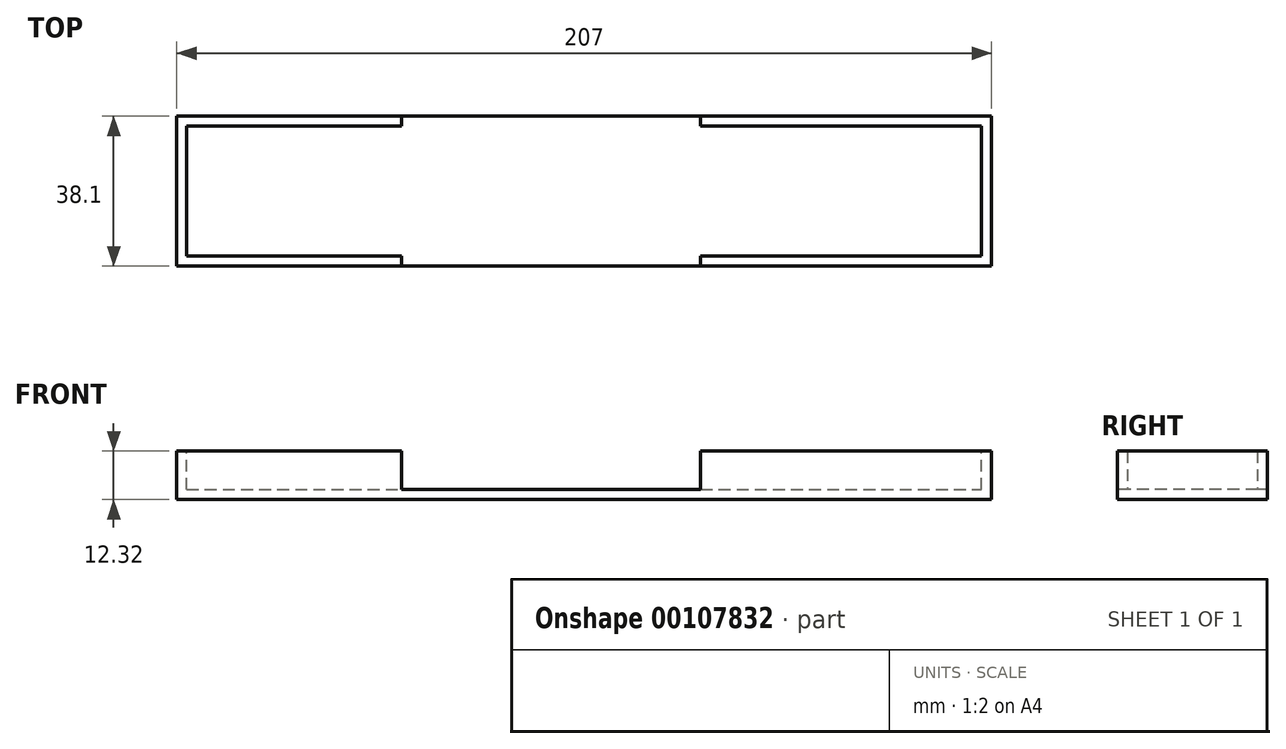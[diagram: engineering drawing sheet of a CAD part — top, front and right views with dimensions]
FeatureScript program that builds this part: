
annotation { "Feature Type Name" : "Feature", "Feature Type Description" : "" }
export const myFeature = defineFeature(function(context is Context, id is Id, definition is map)
    precondition{}
    {
        {
            var Q0;
            Q0=qCreatedBy(makeId("Front.planeOp"),FACE);
            var sketch = newSketch(context, id + "F0", { "sketchPlane" : qUnion([Q0])});
            skLineSegment(sketch, "E0.bottom", {"start": v(103.5, -6.16) * mm, "end": v(-103.5, -6.16) * mm});
            skLineSegment(sketch, "E0.left", {"start": v(103.5, -6.16) * mm, "end": v(103.5, 6.16) * mm});
            skLineSegment(sketch, "E0.right", {"start": v(-103.5, -6.16) * mm, "end": v(-103.5, 6.16) * mm});
            skPoint(sketch, "E0.middle", {"position": v(0, 0) * mm});
            skLineSegment(sketch, "E1", {"start": v(-103.5, 6.16) * mm, "end": v(-46.35, 6.16) * mm});
            skLineSegment(sketch, "E2", {"start": v(-46.35, 6.16) * mm, "end": v(-46.35, -3.62) * mm});
            skLineSegment(sketch, "E3", {"start": v(-46.35, -3.62) * mm, "end": v(29.57, -3.62) * mm});
            skLineSegment(sketch, "E4", {"start": v(29.57, -3.62) * mm, "end": v(29.57, 6.16) * mm});
            skLineSegment(sketch, "E5", {"start": v(29.57, 6.16) * mm, "end": v(103.5, 6.16) * mm});
            skSolve(sketch);
        }
        {
            var Q0;
            Q0 = qSketchRegion(id + "F0", true);
            extrude(context, id + "F1", {"entities" : qUnion([Q0]), "oppositeDirection" : true, "depth" : 38.1 * mm});
        }
        {
            var Q0;
            Q0=makeQuery(id+"F1.opExtrude","SWEPT_FACE",FACE,{"disambiguationData":[OSD([sQuery(id+"F0.wireOp",EDGE,"E1")])]});
            var sketch = newSketch(context, id + "F2", { "sketchPlane" : qUnion([Q0])});
            skLineSegment(sketch, "E6.bottom", {"start": v(-100.97, 35.56) * mm, "end": v(100.97, 35.56) * mm});
            skLineSegment(sketch, "E6.top", {"start": v(-100.97, 2.54) * mm, "end": v(100.97, 2.54) * mm});
            skLineSegment(sketch, "E6.left", {"start": v(-100.97, 35.56) * mm, "end": v(-100.97, 2.54) * mm});
            skLineSegment(sketch, "E6.right", {"start": v(100.97, 35.56) * mm, "end": v(100.97, 2.54) * mm});
            skSolve(sketch);
        }
        {
            var Q0;
            Q0 = qSketchRegion(id + "F2", true);
            extrude(context, id + "F3", {"entities" : qUnion([Q0]), "operationType" : NewBodyOperationType.REMOVE, "oppositeDirection" : true, "depth" : 9.78 * mm});
        }
    });
